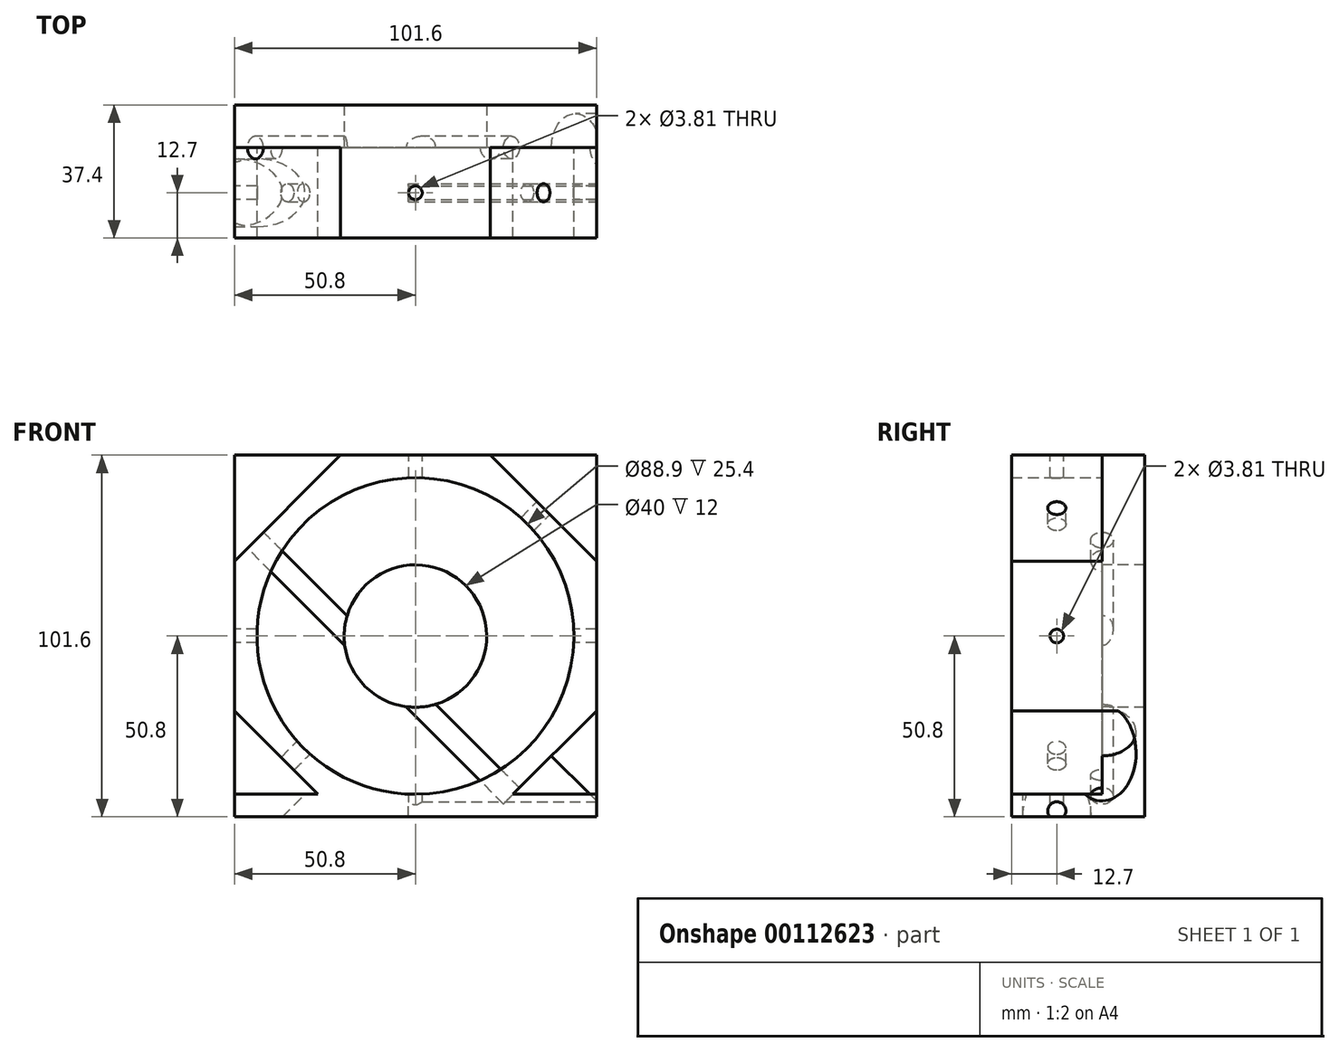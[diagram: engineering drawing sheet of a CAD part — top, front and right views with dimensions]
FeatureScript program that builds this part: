
annotation { "Feature Type Name" : "Feature", "Feature Type Description" : "" }
export const myFeature = defineFeature(function(context is Context, id is Id, definition is map)
    precondition{}
    {
        {
            var Q0;
            Q0=qCreatedBy(makeId("Front.planeOp"),FACE);
            var sketch = newSketch(context, id + "F0", { "sketchPlane" : qUnion([Q0])});
            skCircle(sketch, "E0", {"center": v(0, 0) * mm, "radius": 50.8 * mm, "construction": true});
            skCircle(sketch, "E1", {"center": v(0, 0) * mm, "radius": 44.45 * mm});
            skLineSegment(sketch, "E2.bottom", {"start": v(-50.8, -44.45) * mm, "end": v(50.8, -44.45) * mm});
            skLineSegment(sketch, "E2.top", {"start": v(-50.8, -50.8) * mm, "end": v(50.8, -50.8) * mm});
            skLineSegment(sketch, "E2.left", {"start": v(-50.8, -44.45) * mm, "end": v(-50.8, -50.8) * mm});
            skLineSegment(sketch, "E2.right", {"start": v(50.8, -44.45) * mm, "end": v(50.8, -50.8) * mm});
            skPoint(sketch, "E3", {"position": v(0, -44.45) * mm});
            skLineSegment(sketch, "E4.0", {"start": v(50.8, -21.04) * mm, "end": v(21.04, -50.8) * mm});
            skLineSegment(sketch, "E4.1", {"start": v(21.04, -50.8) * mm, "end": v(-21.04, -50.8) * mm});
            skLineSegment(sketch, "E4.2", {"start": v(-21.04, -50.8) * mm, "end": v(-50.8, -21.04) * mm});
            skLineSegment(sketch, "E4.3", {"start": v(-50.8, -21.04) * mm, "end": v(-50.8, 21.04) * mm});
            skLineSegment(sketch, "E4.4", {"start": v(-50.8, 21.04) * mm, "end": v(-21.04, 50.8) * mm});
            skLineSegment(sketch, "E4.5", {"start": v(-21.04, 50.8) * mm, "end": v(21.04, 50.8) * mm});
            skLineSegment(sketch, "E4.6", {"start": v(21.04, 50.8) * mm, "end": v(50.8, 21.04) * mm});
            skLineSegment(sketch, "E4.7", {"start": v(50.8, 21.04) * mm, "end": v(50.8, -21.04) * mm});
            skPoint(sketch, "E4.0.midPoint", {"position": v(35.92, -35.92) * mm});
            skSolve(sketch);
        }
        {
            var Q0;
            Q0 = qSketchRegion(id + "F0", true);
            extrude(context, id + "F1", {"entities" : qUnion([Q0]), "depth" : 25.4 * mm});
        }
        {
            var Q0;
            Q0=makeQuery(id+"F1.opExtrude","CAP_FACE",FACE,{"disambiguationData":[OSD([sQuery(id+"F0.wireOp",EDGE,"E0"),sQuery(id+"F0.wireOp",EDGE,"E1"),sQuery(id+"F0.wireOp",EDGE,"E2.bottom"),sQuery(id+"F0.wireOp",EDGE,"E2.top"),sQuery(id+"F0.wireOp",EDGE,"E2.left"),sQuery(id+"F0.wireOp",EDGE,"E2.right")])],"isStart":true});
            var sketch = newSketch(context, id + "F2", { "sketchPlane" : qUnion([Q0])});
            skLineSegment(sketch, "E5.bottom", {"start": v(-50.8, 50.8) * mm, "end": v(50.8, 50.8) * mm});
            skLineSegment(sketch, "E5.top", {"start": v(-50.8, -50.8) * mm, "end": v(50.8, -50.8) * mm});
            skLineSegment(sketch, "E5.left", {"start": v(-50.8, 50.8) * mm, "end": v(-50.8, -50.8) * mm});
            skLineSegment(sketch, "E5.right", {"start": v(50.8, 50.8) * mm, "end": v(50.8, -50.8) * mm});
            skCircle(sketch, "E6", {"center": v(0, 0) * mm, "radius": 20 * mm});
            skSolve(sketch);
        }
        {
            var Q0;
            Q0 = qSketchRegion(id + "F2", true);
            extrude(context, id + "F3", {"entities" : qUnion([Q0]), "operationType" : NewBodyOperationType.ADD, "depth" : 12 * mm});
        }
        {
            var Q0;
            Q0=makeQuery(id+"F1.opExtrude","SWEPT_FACE",FACE,{"disambiguationData":[OSD([sQuery(id+"F0.wireOp",EDGE,"E4.6")])]});
            var sketch = newSketch(context, id + "F4", { "sketchPlane" : qUnion([Q0])});
            skLineSegment(sketch, "E7", {"start": v(-12.7, 21.04) * mm, "end": v(-12.7, -21.04) * mm, "construction": true});
            skCircle(sketch, "E8", {"center": v(-12.7, 0) * mm, "radius": 2.55 * mm});
            skSolve(sketch);
        }
        {
            var Q0;
            Q0=makeQuery(id+"F1.opExtrude","SWEPT_FACE",FACE,{"disambiguationData":[OSD([sQuery(id+"F0.wireOp",EDGE,"E4.4")])]});
            var sketch = newSketch(context, id + "F5", { "sketchPlane" : qUnion([Q0])});
            skLineSegment(sketch, "E9", {"start": v(-21.04, -12.7) * mm, "end": v(21.04, -12.7) * mm, "construction": true});
            skCircle(sketch, "E10", {"center": v(0, -12.7) * mm, "radius": 3.18 * mm});
            skSolve(sketch);
        }
        {
            var Q0;
            Q0 = qSketchRegion(id + "F5", true);
            var Q1;
            Q1=makeQuery(id+"F1.opExtrude","SWEPT_FACE",FACE,{"disambiguationData":[OSD([sQuery(id+"F0.wireOp",EDGE,"E4.0")])]});
            extrude(context, id + "F6", {"entities" : qUnion([Q0]), "operationType" : NewBodyOperationType.REMOVE, "endBound" : BoundingType.UP_TO_SURFACE, "oppositeDirection" : true, "endBoundEntityFace" : qUnion([Q1]), "depth" : 25.4 * mm});
        }
        {
            var Q0;
            Q0=makeQuery(id+"F1.opExtrude","SWEPT_FACE",FACE,{"disambiguationData":[OSD([sQuery(id+"F0.wireOp",EDGE,"E4.2")])]});
            var sketch = newSketch(context, id + "F7", { "sketchPlane" : qUnion([Q0])});
            skCircle(sketch, "E11", {"center": v(12.7, 0) * mm, "radius": 9.53 * mm});
            skSolve(sketch);
        }
        {
            var Q0;
            Q0 = qSketchRegion(id + "F7", true);
            var Q1;
            Q1=makeQuery(id+"F3.boolean.opBoolean","MERGE",FACE,{"derivedFrom":[makeQuery(id+"F1.opExtrude","SWEPT_FACE",FACE,{"disambiguationData":[OSD([sQuery(id+"F0.wireOp",EDGE,"E2.top"),sQuery(id+"F0.wireOp",EDGE,"E4.1")])]}),makeQuery(id+"F3.opExtrude","SWEPT_FACE",FACE,{"disambiguationData":[OSD([sQuery(id+"F2.wireOp",EDGE,"E5.top")])]})]});
            extrude(context, id + "F8", {"entities" : qUnion([Q0]), "operationType" : NewBodyOperationType.REMOVE, "endBound" : BoundingType.UP_TO_SURFACE, "endBoundEntityFace" : qUnion([Q1]), "depth" : 25.4 * mm});
        }
        {
            var Q0;
            Q0=makeQuery(id+"F1.opExtrude","SWEPT_FACE",FACE,{"disambiguationData":[OSD([sQuery(id+"F0.wireOp",EDGE,"E4.0")])]});
            var sketch = newSketch(context, id + "F9", { "sketchPlane" : qUnion([Q0])});
            skCircle(sketch, "E12", {"center": v(0, 12.7) * mm, "radius": 9.53 * mm});
            skSolve(sketch);
        }
        {
            var Q0;
            Q0 = qSketchRegion(id + "F9", true);
            var Q1;
            Q1=makeQuery(id+"F3.boolean.opBoolean","MERGE",FACE,{"derivedFrom":[makeQuery(id+"F1.opExtrude","SWEPT_FACE",FACE,{"disambiguationData":[OSD([sQuery(id+"F0.wireOp",EDGE,"E2.top"),sQuery(id+"F0.wireOp",EDGE,"E4.1")])]}),makeQuery(id+"F3.opExtrude","SWEPT_FACE",FACE,{"disambiguationData":[OSD([sQuery(id+"F2.wireOp",EDGE,"E5.top")])]})]});
            extrude(context, id + "F10", {"entities" : qUnion([Q0]), "operationType" : NewBodyOperationType.REMOVE, "endBound" : BoundingType.UP_TO_SURFACE, "endBoundEntityFace" : qUnion([Q1]), "depth" : 25.4 * mm});
        }
        {
            var Q0;
            Q0=makeQuery(id+"F3.boolean.opBoolean","MERGE",FACE,{"derivedFrom":[makeQuery(id+"F1.opExtrude","SWEPT_FACE",FACE,{"disambiguationData":[OSD([sQuery(id+"F0.wireOp",EDGE,"E4.5")])]}),makeQuery(id+"F3.opExtrude","SWEPT_FACE",FACE,{"disambiguationData":[OSD([sQuery(id+"F2.wireOp",EDGE,"E5.bottom")])]})]});
            var sketch = newSketch(context, id + "F11", { "sketchPlane" : qUnion([Q0])});
            skLineSegment(sketch, "E13", {"start": v(-21.04, -12.7) * mm, "end": v(21.04, -12.7) * mm, "construction": true});
            skCircle(sketch, "E14", {"center": v(0, -12.7) * mm, "radius": 1.9 * mm});
            skSolve(sketch);
        }
        {
            var Q0;
            Q0 = qSketchRegion(id + "F11", true);
            var Q1;
            Q1=makeQuery(id+"F3.boolean.opBoolean","MERGE",FACE,{"derivedFrom":[makeQuery(id+"F1.opExtrude","SWEPT_FACE",FACE,{"disambiguationData":[OSD([sQuery(id+"F0.wireOp",EDGE,"E2.top"),sQuery(id+"F0.wireOp",EDGE,"E4.1")])]}),makeQuery(id+"F3.opExtrude","SWEPT_FACE",FACE,{"disambiguationData":[OSD([sQuery(id+"F2.wireOp",EDGE,"E5.top")])]})]});
            extrude(context, id + "F12", {"entities" : qUnion([Q0]), "operationType" : NewBodyOperationType.REMOVE, "endBound" : BoundingType.UP_TO_SURFACE, "oppositeDirection" : true, "endBoundEntityFace" : qUnion([Q1]), "depth" : 25.4 * mm});
        }
        {
            var Q0;
            {var subQ0=sQuery(id+"F2.wireOp",EDGE,"E5.top");var subQ1=sQuery(id+"F2.wireOp",EDGE,"E6");var subQ2=sQuery(id+"F2.wireOp",EDGE,"E5.right");var subQ3=sQuery(id+"F2.wireOp",EDGE,"E5.left");var subQ4=sQuery(id+"F2.wireOp",EDGE,"E5.bottom");var subQ5=sQuery(id+"F0.wireOp",EDGE,"E4.4");var subQ6=sQuery(id+"F0.wireOp",EDGE,"E4.5");var subQ7=sQuery(id+"F0.wireOp",EDGE,"E4.3");var subQ8=sQuery(id+"F0.wireOp",EDGE,"E4.2");var subQ9=sQuery(id+"F0.wireOp",EDGE,"E4.1");var subQ10=sQuery(id+"F0.wireOp",EDGE,"E2.left");var subQ11=sQuery(id+"F0.wireOp",EDGE,"E2.top");var subQ12=sQuery(id+"F0.wireOp",EDGE,"E2.bottom");Q0=makeQuery(id+"F8.boolean.opBoolean","SPLIT",FACE,{"disambiguationData":[TD([makeQuery(id+"F1.opExtrude","CAP_FACE",FACE,{"disambiguationData":[OSD([sQuery(id+"F0.wireOp",EDGE,"E1"),subQ12,subQ11,subQ10,sQuery(id+"F0.wireOp",EDGE,"E2.right"),sQuery(id+"F0.wireOp",EDGE,"E4.0"),subQ9,subQ8,subQ7,subQ5,subQ6,sQuery(id+"F0.wireOp",EDGE,"E4.6"),sQuery(id+"F0.wireOp",EDGE,"E4.7")])],"isStart":false}),makeQuery(id+"F1.opExtrude","SWEPT_FACE",FACE,{"disambiguationData":[OSD([subQ12]),TDD([makeQuery(id+"F0.imprint","IMPRINT",EDGE,{"disambiguationData":[TD([[makeQuery(id+"F0.imprint","INTERSECT",VERTEX,{"derivedFrom":[subQ12,subQ10]}),-1.0]])],"derivedFrom":subQ12})])]}),makeQuery(id+"F1.opExtrude","SWEPT_FACE",FACE,{"disambiguationData":[OSD([subQ11,subQ9])]}),makeQuery(id+"F1.opExtrude","SWEPT_FACE",FACE,{"disambiguationData":[OSD([subQ8])]}),makeQuery(id+"F1.opExtrude","SWEPT_FACE",FACE,{"disambiguationData":[OSD([subQ5])]}),makeQuery(id+"F1.opExtrude","SWEPT_FACE",FACE,{"disambiguationData":[OSD([subQ6])]}),makeQuery(id+"F3.opExtrude","SWEPT_FACE",FACE,{"disambiguationData":[OSD([subQ4])]}),makeQuery(id+"F3.opExtrude","CAP_FACE",FACE,{"disambiguationData":[OSD([subQ4,subQ0,subQ3,subQ2,subQ1])],"isStart":true}),makeQuery(id+"F3.opExtrude","CAP_FACE",FACE,{"disambiguationData":[OSD([subQ4,subQ0,subQ3,subQ2,subQ1])],"isStart":false}),makeQuery(id+"F3.opExtrude","SWEPT_FACE",FACE,{"disambiguationData":[OSD([subQ0])]}),makeQuery(id+"F8.opExtrude","SWEPT_FACE",FACE,{"disambiguationData":[OSD([sQuery(id+"F7.wireOp",EDGE,"E11")])]})])],"derivedFrom":makeQuery(id+"F3.boolean.opBoolean","MERGE",FACE,{"derivedFrom":[makeQuery(id+"F1.opExtrude","SWEPT_FACE",FACE,{"disambiguationData":[OSD([subQ10])]}),makeQuery(id+"F1.opExtrude","SWEPT_FACE",FACE,{"disambiguationData":[OSD([subQ7])]}),makeQuery(id+"F3.opExtrude","SWEPT_FACE",FACE,{"disambiguationData":[OSD([subQ2])]})]})});}
            var sketch = newSketch(context, id + "F13", { "sketchPlane" : qUnion([Q0])});
            skLineSegment(sketch, "E15", {"start": v(12.7, 21.04) * mm, "end": v(12.7, -21.04) * mm, "construction": true});
            skCircle(sketch, "E16", {"center": v(12.7, 0) * mm, "radius": 1.9 * mm});
            skSolve(sketch);
        }
        {
            var Q0;
            Q0 = qSketchRegion(id + "F13", true);
            var Q1;
            {var subQ0=sQuery(id+"F2.wireOp",EDGE,"E5.top");var subQ1=sQuery(id+"F2.wireOp",EDGE,"E6");var subQ2=sQuery(id+"F2.wireOp",EDGE,"E5.right");var subQ3=sQuery(id+"F2.wireOp",EDGE,"E5.left");var subQ4=sQuery(id+"F2.wireOp",EDGE,"E5.bottom");var subQ5=sQuery(id+"F0.wireOp",EDGE,"E4.6");var subQ6=sQuery(id+"F0.wireOp",EDGE,"E4.7");var subQ7=sQuery(id+"F0.wireOp",EDGE,"E4.5");var subQ8=sQuery(id+"F0.wireOp",EDGE,"E4.1");var subQ9=sQuery(id+"F0.wireOp",EDGE,"E4.0");var subQ10=sQuery(id+"F0.wireOp",EDGE,"E2.right");var subQ11=sQuery(id+"F0.wireOp",EDGE,"E2.top");var subQ12=sQuery(id+"F0.wireOp",EDGE,"E2.bottom");Q1=makeQuery(id+"F10.boolean.opBoolean","SPLIT",FACE,{"disambiguationData":[TD([makeQuery(id+"F1.opExtrude","CAP_FACE",FACE,{"disambiguationData":[OSD([sQuery(id+"F0.wireOp",EDGE,"E1"),subQ12,subQ11,sQuery(id+"F0.wireOp",EDGE,"E2.left"),subQ10,subQ9,subQ8,sQuery(id+"F0.wireOp",EDGE,"E4.2"),sQuery(id+"F0.wireOp",EDGE,"E4.3"),sQuery(id+"F0.wireOp",EDGE,"E4.4"),subQ7,subQ5,subQ6])],"isStart":false}),makeQuery(id+"F1.opExtrude","SWEPT_FACE",FACE,{"disambiguationData":[OSD([subQ12]),TDD([makeQuery(id+"F0.imprint","IMPRINT",EDGE,{"disambiguationData":[TD([[makeQuery(id+"F0.imprint","INTERSECT",VERTEX,{"derivedFrom":[subQ12,subQ10]}),1.0]])],"derivedFrom":subQ12})])]}),makeQuery(id+"F1.opExtrude","SWEPT_FACE",FACE,{"disambiguationData":[OSD([subQ11,subQ8])]}),makeQuery(id+"F1.opExtrude","SWEPT_FACE",FACE,{"disambiguationData":[OSD([subQ9])]}),makeQuery(id+"F1.opExtrude","SWEPT_FACE",FACE,{"disambiguationData":[OSD([subQ7])]}),makeQuery(id+"F1.opExtrude","SWEPT_FACE",FACE,{"disambiguationData":[OSD([subQ5])]}),makeQuery(id+"F3.opExtrude","SWEPT_FACE",FACE,{"disambiguationData":[OSD([subQ4])]}),makeQuery(id+"F3.opExtrude","CAP_FACE",FACE,{"disambiguationData":[OSD([subQ4,subQ0,subQ3,subQ2,subQ1])],"isStart":true}),makeQuery(id+"F3.opExtrude","CAP_FACE",FACE,{"disambiguationData":[OSD([subQ4,subQ0,subQ3,subQ2,subQ1])],"isStart":false}),makeQuery(id+"F3.opExtrude","SWEPT_FACE",FACE,{"disambiguationData":[OSD([subQ0])]}),makeQuery(id+"F10.opExtrude","SWEPT_FACE",FACE,{"disambiguationData":[OSD([sQuery(id+"F9.wireOp",EDGE,"E12")])]})])],"derivedFrom":makeQuery(id+"F3.boolean.opBoolean","MERGE",FACE,{"derivedFrom":[makeQuery(id+"F1.opExtrude","SWEPT_FACE",FACE,{"disambiguationData":[OSD([subQ10])]}),makeQuery(id+"F1.opExtrude","SWEPT_FACE",FACE,{"disambiguationData":[OSD([subQ6])]}),makeQuery(id+"F3.opExtrude","SWEPT_FACE",FACE,{"disambiguationData":[OSD([subQ3])]})]})});}
            extrude(context, id + "F14", {"entities" : qUnion([Q0]), "operationType" : NewBodyOperationType.REMOVE, "endBound" : BoundingType.UP_TO_SURFACE, "oppositeDirection" : true, "endBoundEntityFace" : qUnion([Q1]), "depth" : 25.4 * mm});
        }
        {
            var Q0;
            Q0=makeQuery(id+"F3.boolean.opBoolean","MERGE",FACE,{"derivedFrom":[makeQuery(id+"F1.opExtrude","SWEPT_FACE",FACE,{"disambiguationData":[OSD([sQuery(id+"F0.wireOp",EDGE,"E2.top"),sQuery(id+"F0.wireOp",EDGE,"E4.1")])]}),makeQuery(id+"F3.opExtrude","SWEPT_FACE",FACE,{"disambiguationData":[OSD([sQuery(id+"F2.wireOp",EDGE,"E5.top")])]})]});
            var sketch = newSketch(context, id + "F15", { "sketchPlane" : qUnion([Q0])});
            skLineSegment(sketch, "E17", {"start": v(50.8, 14.6) * mm, "end": v(0, 14.6) * mm, "construction": true});
            skLineSegment(sketch, "E18", {"start": v(50.8, 10.8) * mm, "end": v(0, 10.8) * mm, "construction": true});
            skSolve(sketch);
        }
        {
            var Q0;
            Q0=makeQuery(id+"F3.boolean.opBoolean","MERGE",FACE,{"derivedFrom":[makeQuery(id+"F1.opExtrude","SWEPT_FACE",FACE,{"disambiguationData":[OSD([sQuery(id+"F0.wireOp",EDGE,"E2.right")])]}),makeQuery(id+"F1.opExtrude","SWEPT_FACE",FACE,{"disambiguationData":[OSD([sQuery(id+"F0.wireOp",EDGE,"E4.7")])]}),makeQuery(id+"F3.opExtrude","SWEPT_FACE",FACE,{"disambiguationData":[OSD([sQuery(id+"F2.wireOp",EDGE,"E5.left")])]})]});
            var sketch = newSketch(context, id + "F16", { "sketchPlane" : qUnion([Q0])});
            skArc(sketch, "E19", {"start": v(-10.8, -50.8) * mm, "mid": v(-12.7, -46.58) * mm, "end": v(-14.6, -50.8) * mm});
            skLineSegment(sketch, "E20", {"start": v(-14.6, -50.8) * mm, "end": v(-10.8, -50.8) * mm});
            skSolve(sketch);
        }
        {
            var Q0;
            Q0 = qSketchRegion(id + "F16", true);
            var Q1;
            Q1=makeQuery(id+"F12.boolean.opBoolean","COPY",FACE,{"disambiguationData":[OD(0.0)],"derivedFrom":makeQuery(id+"F12.opExtrude","SWEPT_FACE",FACE,{"disambiguationData":[OSD([sQuery(id+"F11.wireOp",EDGE,"E14")])]})});
            extrude(context, id + "F17", {"entities" : qUnion([Q0]), "operationType" : NewBodyOperationType.REMOVE, "oppositeDirection" : true, "endBoundEntityFace" : qUnion([Q1]), "depth" : 52.83 * mm});
        }
        {
            var Q0;
            Q0 = qSketchRegion(id + "F4", true);
            var Q1;
            Q1=makeQuery(id+"F1.opExtrude","SWEPT_FACE",FACE,{"disambiguationData":[OSD([sQuery(id+"F0.wireOp",EDGE,"E4.2")])]});
            extrude(context, id + "F18", {"entities" : qUnion([Q0]), "operationType" : NewBodyOperationType.REMOVE, "endBound" : BoundingType.UP_TO_SURFACE, "oppositeDirection" : true, "endBoundEntityFace" : qUnion([Q1]), "depth" : 25.4 * mm});
        }
    });
